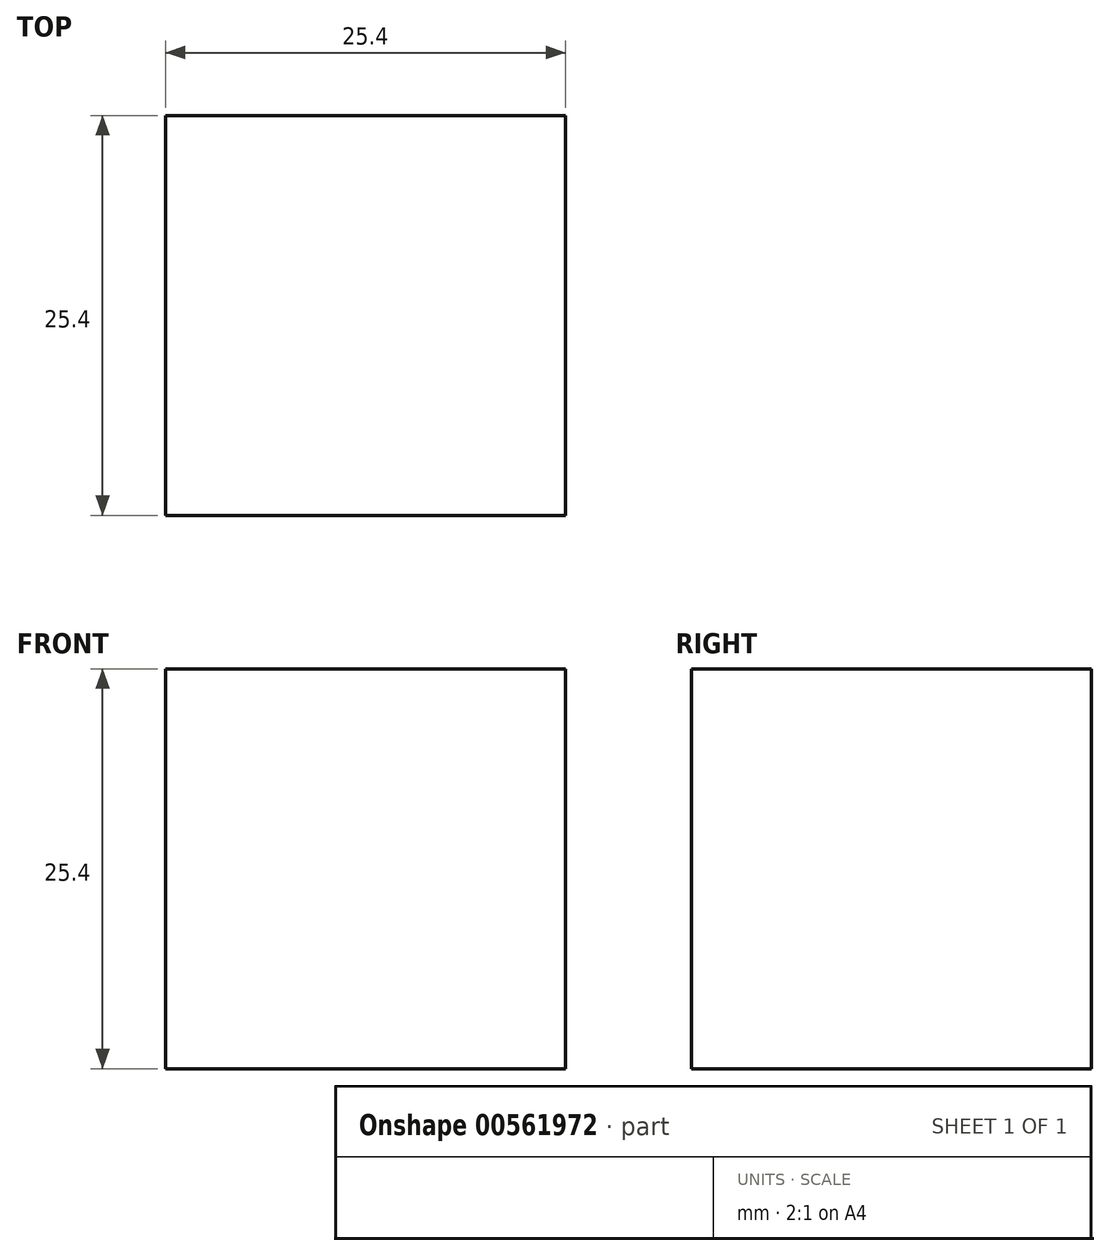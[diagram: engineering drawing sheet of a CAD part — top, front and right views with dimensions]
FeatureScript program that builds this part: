
annotation { "Feature Type Name" : "Feature", "Feature Type Description" : "" }
export const myFeature = defineFeature(function(context is Context, id is Id, definition is map)
    precondition{}
    {
        {
            var Q0;
            Q0=qCreatedBy(makeId("Front.planeOp"),FACE);
            var sketch = newSketch(context, id + "F0", { "sketchPlane" : qUnion([Q0])});
            skLineSegment(sketch, "E0.bottom", {"start": v(-43.82, 44.59) * mm, "end": v(-18.42, 44.59) * mm});
            skLineSegment(sketch, "E0.top", {"start": v(-43.82, 19.19) * mm, "end": v(-18.42, 19.19) * mm});
            skLineSegment(sketch, "E0.left", {"start": v(-43.82, 44.59) * mm, "end": v(-43.82, 19.19) * mm});
            skLineSegment(sketch, "E0.right", {"start": v(-18.42, 44.59) * mm, "end": v(-18.42, 19.19) * mm});
            skSolve(sketch);
        }
        {
            var Q0;
            Q0=makeQuery(id+"F0.imprint","IMPRINT",FACE,{"disambiguationData":[TD([[makeQuery(id+"F0.imprint","IMPRINT",EDGE,{"derivedFrom":sQuery(id+"F0.wireOp",EDGE,"E0.bottom")}),-1.0]])]});
            extrude(context, id + "F1", {"entities" : qUnion([Q0]), "depth" : 25.4 * mm, "offsetDistance" : 25.4 * mm});
        }
    });
